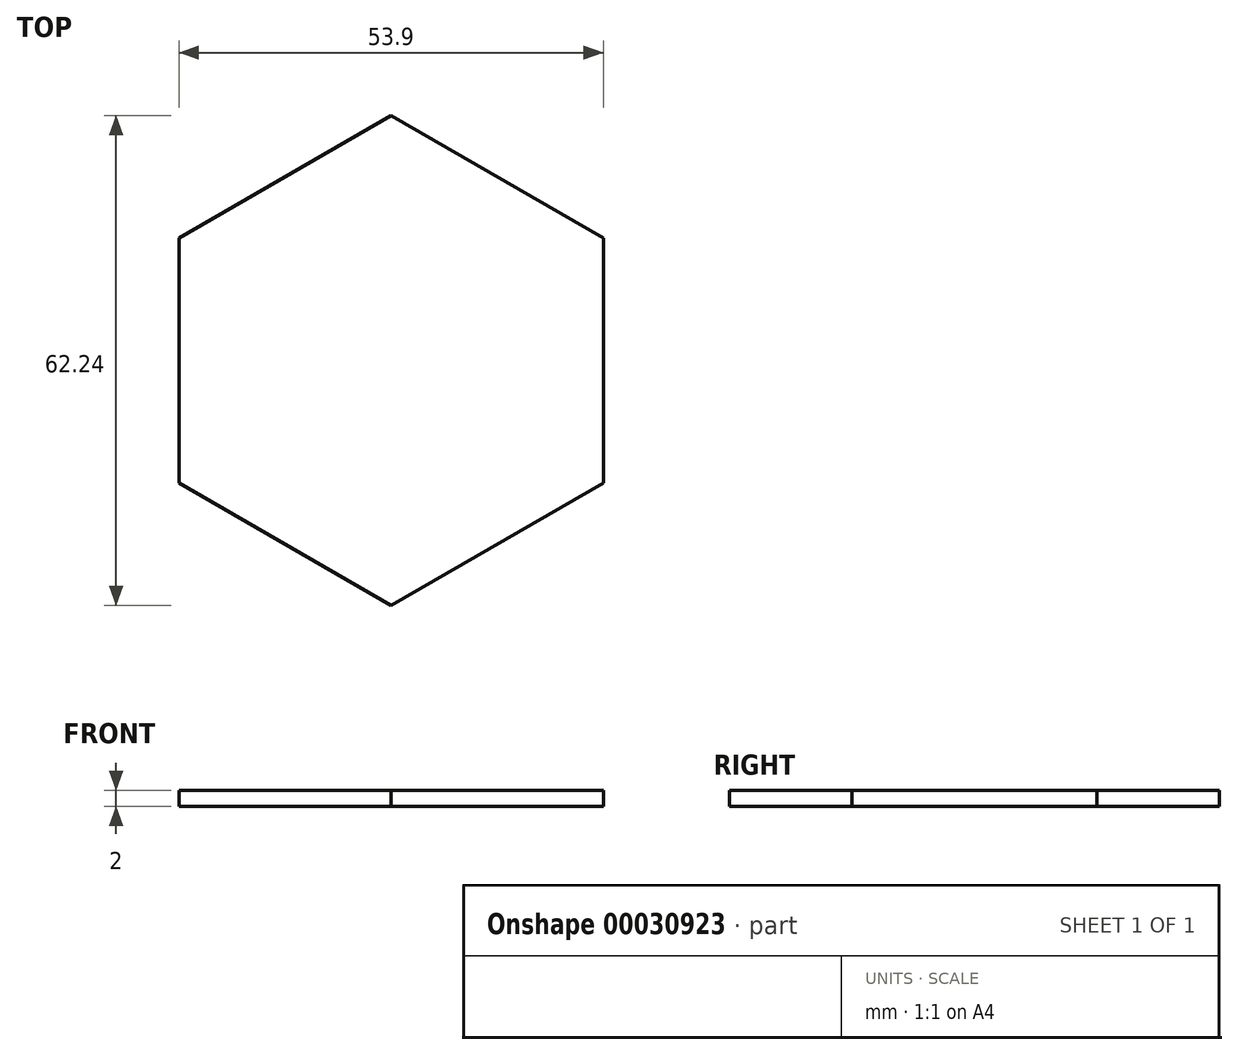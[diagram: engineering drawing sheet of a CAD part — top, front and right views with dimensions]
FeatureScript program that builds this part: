
annotation { "Feature Type Name" : "Feature", "Feature Type Description" : "" }
export const myFeature = defineFeature(function(context is Context, id is Id, definition is map)
    precondition{}
    {
        {
            var Q0;
            Q0=qCreatedBy(makeId("Top.planeOp"),FACE);
            var sketch = newSketch(context, id + "F0", { "sketchPlane" : qUnion([Q0])});
            skCircle(sketch, "E0.cCircle", {"center": v(-8.05, 2.02) * mm, "radius": 26.95 * mm, "construction": true});
            skLineSegment(sketch, "E0.0", {"start": v(18.9, 17.58) * mm, "end": v(18.9, -13.54) * mm});
            skLineSegment(sketch, "E0.1", {"start": v(18.9, -13.54) * mm, "end": v(-8.05, -29.1) * mm});
            skLineSegment(sketch, "E0.2", {"start": v(-8.05, -29.1) * mm, "end": v(-35, -13.54) * mm});
            skLineSegment(sketch, "E0.3", {"start": v(-35, -13.54) * mm, "end": v(-35, 17.58) * mm});
            skLineSegment(sketch, "E0.4", {"start": v(-35, 17.58) * mm, "end": v(-8.05, 33.14) * mm});
            skLineSegment(sketch, "E0.5", {"start": v(-8.05, 33.14) * mm, "end": v(18.9, 17.58) * mm});
            skPoint(sketch, "E0.0.midPoint", {"position": v(18.9, 2.02) * mm});
            skCircle(sketch, "E1", {"center": v(-8.05, 2.02) * mm, "radius": 22.36 * mm});
            skSolve(sketch);
        }
        {
            var Q0;
            Q0=makeQuery(id+"F0.imprint","IMPRINT",FACE,{"disambiguationData":[TD([[makeQuery(id+"F0.imprint","IMPRINT",EDGE,{"derivedFrom":sQuery(id+"F0.wireOp",EDGE,"E0.0")}),-1.0]])]});
            var Q1;
            Q1=makeQuery(id+"F0.imprint","IMPRINT",FACE,{"disambiguationData":[TD([[makeQuery(id+"F0.imprint","IMPRINT",EDGE,{"derivedFrom":sQuery(id+"F0.wireOp",EDGE,"E1")}),1.0]])]});
            extrude(context, id + "F1", {"entities" : qUnion([Q0, Q1]), "depth" : 2 * mm});
        }
    });
